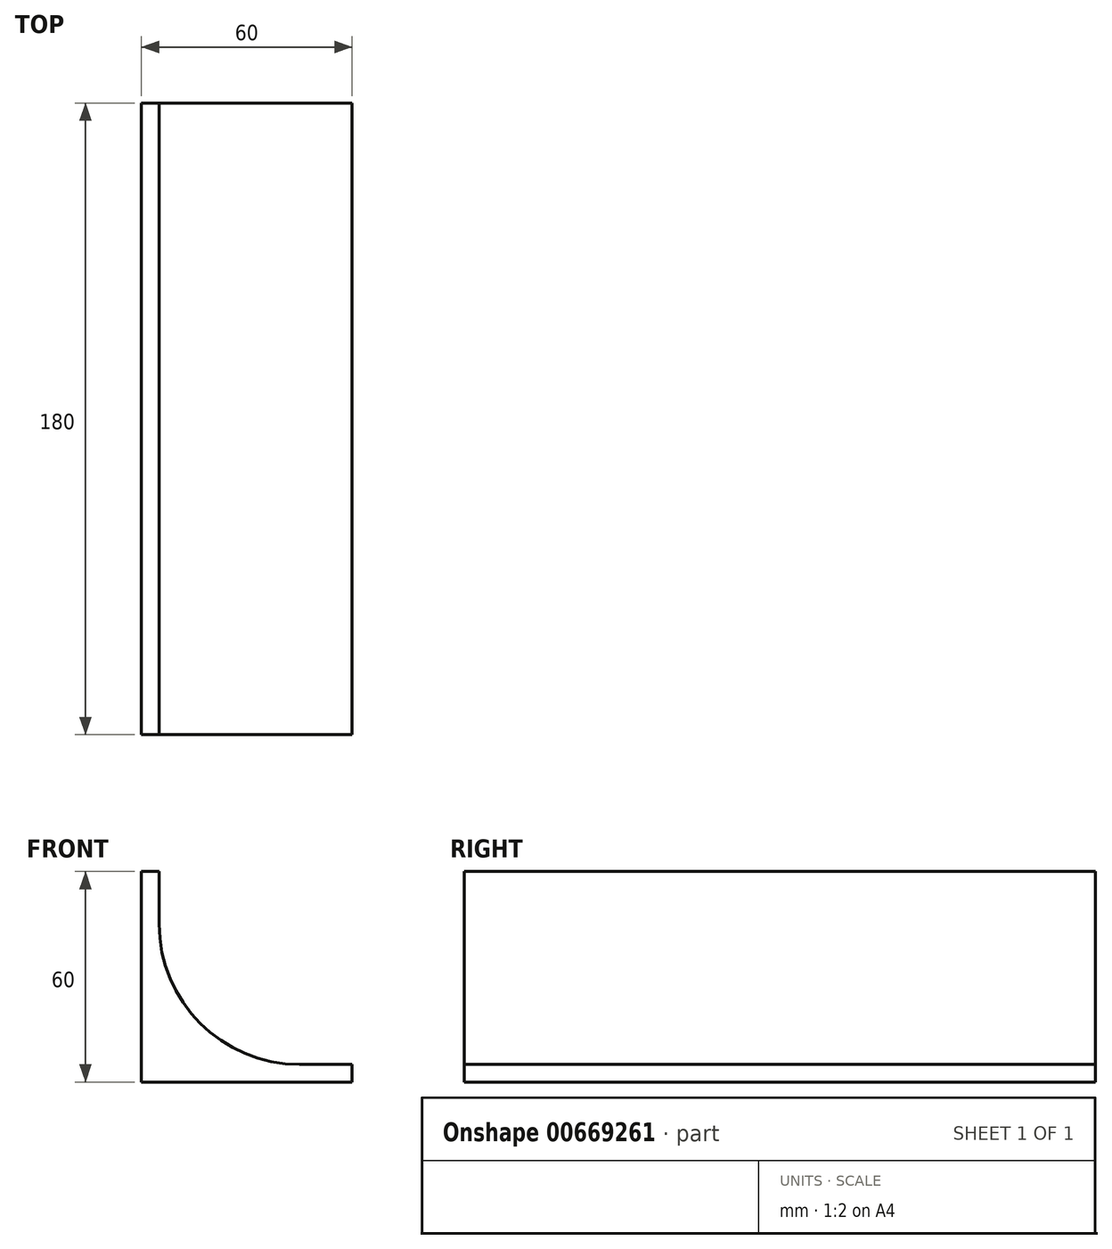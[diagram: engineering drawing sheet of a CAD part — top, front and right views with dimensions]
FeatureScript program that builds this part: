
annotation { "Feature Type Name" : "Feature", "Feature Type Description" : "" }
export const myFeature = defineFeature(function(context is Context, id is Id, definition is map)
    precondition{}
    {
        {
            var Q0;
            Q0=qCreatedBy(makeId("Front.planeOp"),FACE);
            var sketch = newSketch(context, id + "F0", { "sketchPlane" : qUnion([Q0])});
            skLineSegment(sketch, "E0", {"start": v(-60, 60) * mm, "end": v(-60, 0) * mm});
            skLineSegment(sketch, "E1", {"start": v(-60, 0) * mm, "end": v(0, 0) * mm});
            skLineSegment(sketch, "E2", {"start": v(0, 5) * mm, "end": v(-55, 5) * mm});
            skLineSegment(sketch, "E3", {"start": v(-55, 5) * mm, "end": v(-55, 60) * mm});
            skLineSegment(sketch, "E4", {"start": v(-55, 60) * mm, "end": v(-60, 60) * mm});
            skLineSegment(sketch, "E5", {"start": v(0, 0) * mm, "end": v(0, 5) * mm});
            skSolve(sketch);
        }
        {
            var Q0;
            Q0=makeQuery(id+"F0.imprint","IMPRINT",FACE,{"disambiguationData":[TD([[makeQuery(id+"F0.imprint","IMPRINT",EDGE,{"derivedFrom":sQuery(id+"F0.wireOp",EDGE,"E0")}),1.0]])]});
            extrude(context, id + "F1", {"entities" : qUnion([Q0]), "depth" : 180 * mm, "offsetDistance" : 25 * mm});
        }
        {
            var Q0;
            Q0=makeQuery(id+"F1.opExtrude","SWEPT_EDGE",EDGE,{"disambiguationData":[OSD([sQuery(id+"F0.wireOp",EDGE,"E2"),sQuery(id+"F0.wireOp",EDGE,"E3")])]});
            fillet(context, id + "F2", {"entities" : qUnion([Q0]), "radius" : 40 * mm, "tangentPropagation" : true, "allowEdgeOverflow" : false});
        }
    });
